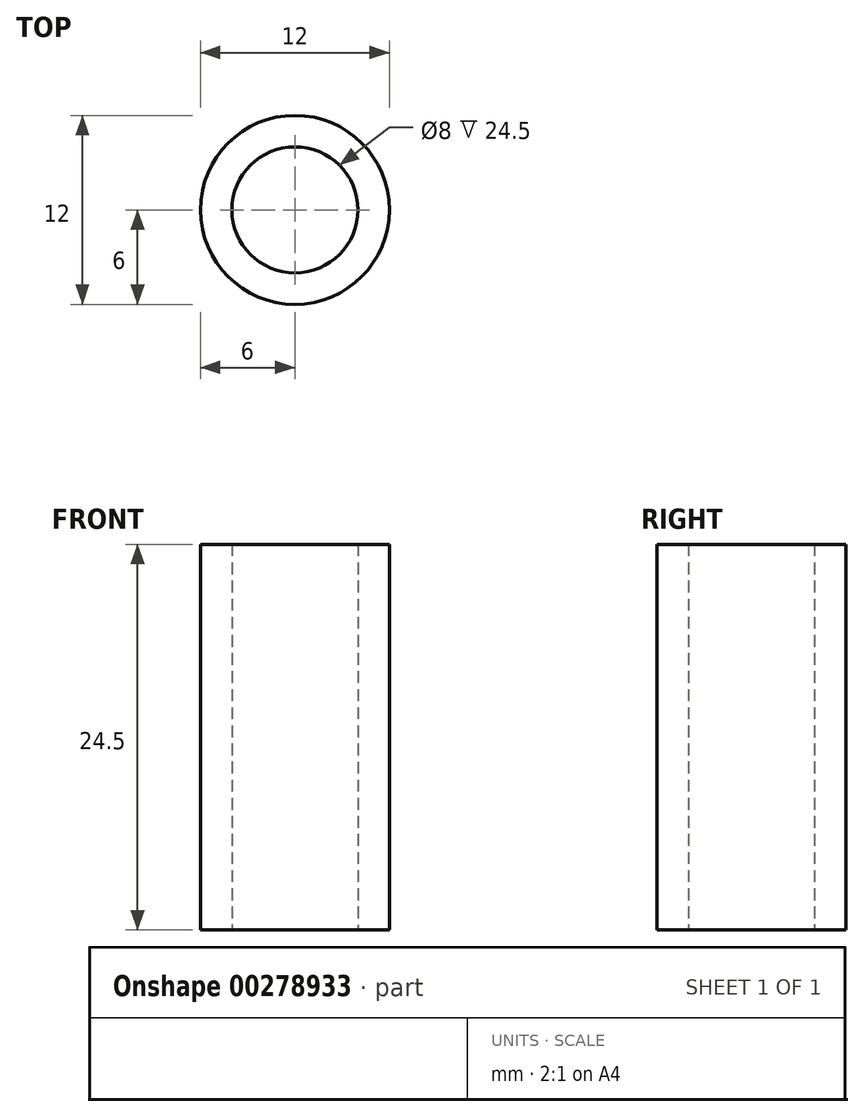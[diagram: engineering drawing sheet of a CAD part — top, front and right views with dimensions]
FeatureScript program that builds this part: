
annotation { "Feature Type Name" : "Feature", "Feature Type Description" : "" }
export const myFeature = defineFeature(function(context is Context, id is Id, definition is map)
    precondition{}
    {
        {
            var Q0;
            Q0=qCreatedBy(makeId("Top.planeOp"),FACE);
            var sketch = newSketch(context, id + "F0", { "sketchPlane" : qUnion([Q0])});
            skCircle(sketch, "E0", {"center": v(0, 0) * mm, "radius": 4 * mm});
            skCircle(sketch, "E1", {"center": v(0, 0) * mm, "radius": 6 * mm});
            skSolve(sketch);
        }
        {
            assignVariable(context, id + "F1", {"name" : "Height", "anyValue" : 24.5});
        }
        {
            var Q0;
            Q0=makeQuery(id+"F0.imprint","IMPRINT",FACE,{"disambiguationData":[TD([[makeQuery(id+"F0.imprint","IMPRINT",EDGE,{"derivedFrom":sQuery(id+"F0.wireOp",EDGE,"E0")}),-1.0]])]});
            extrude(context, id + "F2", {"entities" : qUnion([Q0]), "depth" : getVariable(context, 'Height') * mm});
        }
    });
